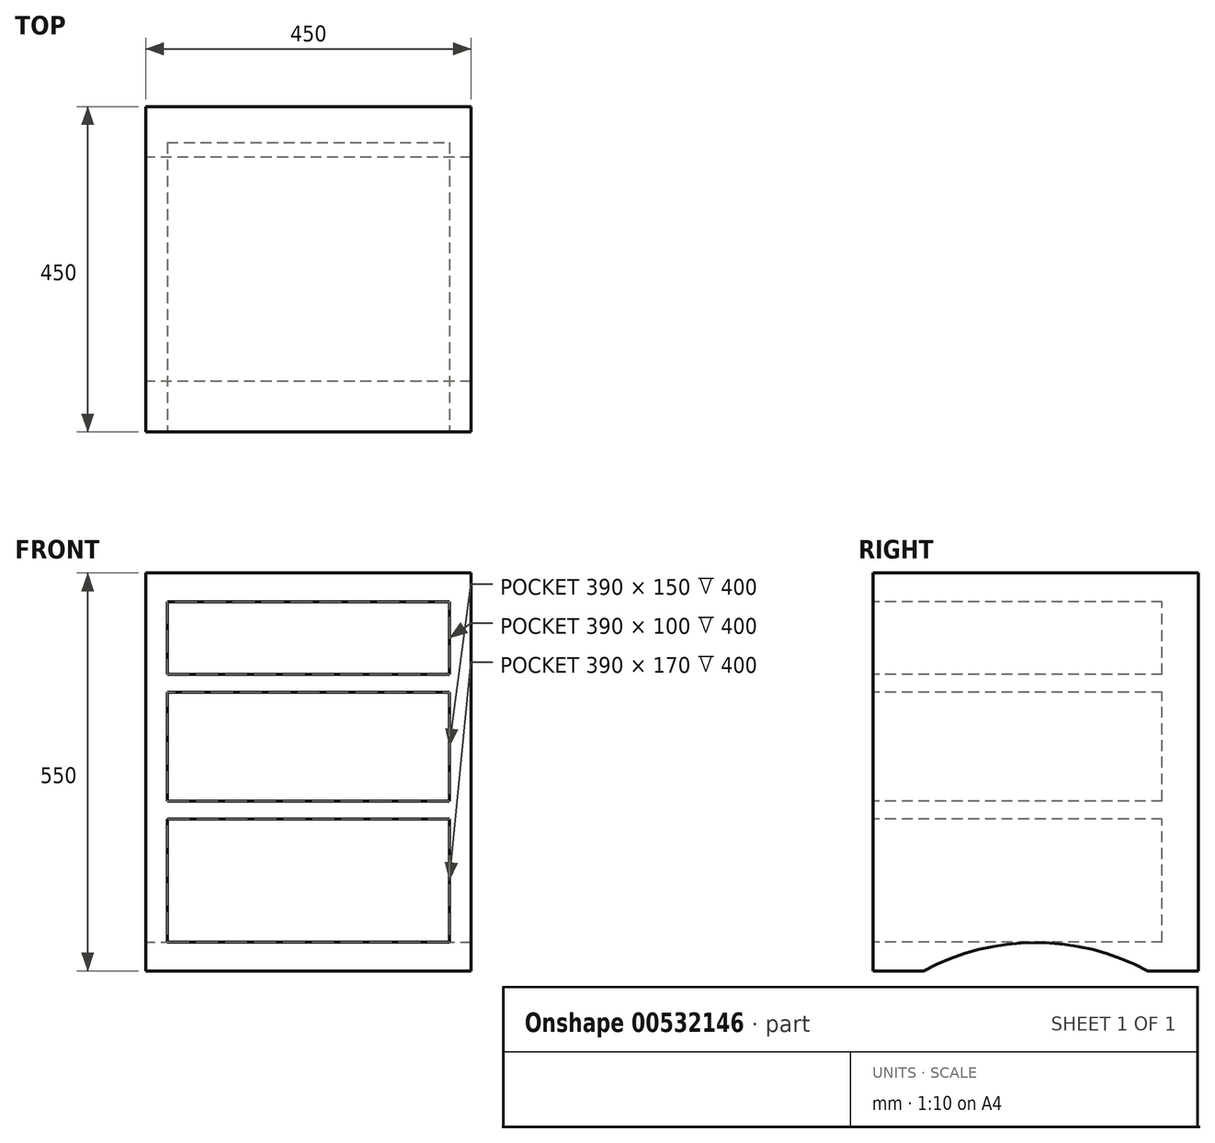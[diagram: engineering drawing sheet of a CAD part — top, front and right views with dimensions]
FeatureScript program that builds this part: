
annotation { "Feature Type Name" : "Feature", "Feature Type Description" : "" }
export const myFeature = defineFeature(function(context is Context, id is Id, definition is map)
    precondition{}
    {
        {
            var Q0;
            Q0=qCreatedBy(makeId("Right.planeOp"),FACE);
            var sketch = newSketch(context, id + "F0", { "sketchPlane" : qUnion([Q0])});
            skLineSegment(sketch, "E0.top", {"start": v(266.1, 549.82) * mm, "end": v(-183.9, 549.82) * mm});
            skLineSegment(sketch, "E0.left", {"start": v(266.1, -0.18) * mm, "end": v(266.1, 549.82) * mm});
            skLineSegment(sketch, "E0.right", {"start": v(-183.9, -0.18) * mm, "end": v(-183.9, 549.82) * mm});
            skArc(sketch, "E1", {"start": v(196.1, -0.18) * mm, "mid": v(41.1, 39.03) * mm, "end": v(-113.9, -0.18) * mm});
            skLineSegment(sketch, "E2", {"start": v(-183.9, -0.18) * mm, "end": v(-113.9, -0.18) * mm});
            skLineSegment(sketch, "E3", {"start": v(196.1, -0.18) * mm, "end": v(266.1, -0.18) * mm});
            skSolve(sketch);
        }
        {
            var Q0;
            Q0=makeQuery(id+"F0.imprint","IMPRINT",FACE,{"disambiguationData":[TD([[makeQuery(id+"F0.imprint","IMPRINT",EDGE,{"derivedFrom":sQuery(id+"F0.wireOp",EDGE,"E0.top")}),1.0]])]});
            extrude(context, id + "F1", {"entities" : qUnion([Q0]), "depth" : 450 * mm, "offsetDistance" : 25 * mm});
        }
        {
            var Q0;
            Q0=makeQuery(id+"F1.opExtrude","SWEPT_FACE",FACE,{"disambiguationData":[OSD([sQuery(id+"F0.wireOp",EDGE,"E0.right")])]});
            var sketch = newSketch(context, id + "F2", { "sketchPlane" : qUnion([Q0])});
            skLineSegment(sketch, "E4.bottom", {"start": v(420, 39.82) * mm, "end": v(30, 39.82) * mm});
            skLineSegment(sketch, "E4.top", {"start": v(420, 509.82) * mm, "end": v(30, 509.82) * mm});
            skLineSegment(sketch, "E4.left", {"start": v(420, 39.82) * mm, "end": v(420, 509.82) * mm});
            skLineSegment(sketch, "E4.right", {"start": v(30, 39.82) * mm, "end": v(30, 509.82) * mm});
            skPoint(sketch, "E4.middle", {"position": v(225, 274.82) * mm});
            skPoint(sketch, "E4.middle.positionSnap0", {"position": v(0, 274.82) * mm});
            skPoint(sketch, "E4.middle.positionSnap1", {"position": v(225, 549.82) * mm});
            skPoint(sketch, "E4.centerSnap0", {"position": v(0, 274.82) * mm});
            skPoint(sketch, "E4.centerSnap1", {"position": v(225, 549.82) * mm});
            skSolve(sketch);
        }
        {
            var Q0;
            Q0=makeQuery(id+"F2.imprint","IMPRINT",FACE,{"disambiguationData":[TD([[makeQuery(id+"F2.imprint","IMPRINT",EDGE,{"derivedFrom":sQuery(id+"F2.wireOp",EDGE,"E4.bottom")}),-1.0]])]});
            extrude(context, id + "F3", {"entities" : qUnion([Q0]), "operationType" : NewBodyOperationType.REMOVE, "oppositeDirection" : true, "depth" : 400 * mm, "offsetDistance" : 25 * mm});
        }
        {
            var Q0;
            Q0=makeQuery(id+"F3.boolean.opBoolean","COPY",FACE,{"derivedFrom":makeQuery(id+"F3.opExtrude","SWEPT_FACE",FACE,{"disambiguationData":[OSD([sQuery(id+"F2.wireOp",EDGE,"E4.left")])]})});
            var sketch = newSketch(context, id + "F4", { "sketchPlane" : qUnion([Q0])});
            skLineSegment(sketch, "E5.bottom", {"start": v(-216.1, 409.82) * mm, "end": v(183.9, 409.82) * mm});
            skLineSegment(sketch, "E5.top", {"start": v(-216.1, 384.82) * mm, "end": v(183.9, 384.82) * mm});
            skLineSegment(sketch, "E5.left", {"start": v(-216.1, 409.82) * mm, "end": v(-216.1, 384.82) * mm});
            skLineSegment(sketch, "E5.right", {"start": v(183.9, 409.82) * mm, "end": v(183.9, 384.82) * mm});
            skLineSegment(sketch, "E6.bottom", {"start": v(-216.1, 234.82) * mm, "end": v(183.9, 234.82) * mm});
            skLineSegment(sketch, "E6.top", {"start": v(-216.1, 209.82) * mm, "end": v(183.9, 209.82) * mm});
            skLineSegment(sketch, "E6.left", {"start": v(-216.1, 234.82) * mm, "end": v(-216.1, 209.82) * mm});
            skLineSegment(sketch, "E6.right", {"start": v(183.9, 234.82) * mm, "end": v(183.9, 209.82) * mm});
            skSolve(sketch);
        }
        {
            var Q0;
            Q0=makeQuery(id+"F4.imprint","IMPRINT",FACE,{"disambiguationData":[TD([[makeQuery(id+"F4.imprint","IMPRINT",EDGE,{"derivedFrom":sQuery(id+"F4.wireOp",EDGE,"E5.bottom")}),-1.0]])]});
            extrude(context, id + "F5", {"entities" : qUnion([Q0]), "operationType" : NewBodyOperationType.ADD, "depth" : 390 * mm, "offsetDistance" : 25 * mm});
        }
        {
            var Q0;
            {var subQ0=sQuery(id+"F2.wireOp",EDGE,"E4.left");var subQ1=sQuery(id+"F2.wireOp",EDGE,"E4.bottom");Q0=makeQuery(id+"F5.boolean.opBoolean","SPLIT",FACE,{"disambiguationData":[TD([makeQuery(id+"F3.boolean.opBoolean","COPY",FACE,{"derivedFrom":makeQuery(id+"F3.opExtrude","SWEPT_FACE",FACE,{"disambiguationData":[OSD([subQ1])]})})])],"derivedFrom":makeQuery(id+"F3.boolean.opBoolean","COPY",FACE,{"derivedFrom":makeQuery(id+"F3.opExtrude","SWEPT_FACE",FACE,{"disambiguationData":[OSD([subQ0])]})})});}
            var sketch = newSketch(context, id + "F6", { "sketchPlane" : qUnion([Q0])});
            skLineSegment(sketch, "E7.bottom", {"start": v(-216.1, 234.82) * mm, "end": v(183.9, 234.82) * mm});
            skLineSegment(sketch, "E7.top", {"start": v(-216.1, 209.82) * mm, "end": v(183.9, 209.82) * mm});
            skLineSegment(sketch, "E7.left", {"start": v(-216.1, 234.82) * mm, "end": v(-216.1, 209.82) * mm});
            skLineSegment(sketch, "E7.right", {"start": v(183.9, 234.82) * mm, "end": v(183.9, 209.82) * mm});
            skSolve(sketch);
        }
        {
            var Q0;
            Q0=makeQuery(id+"F6.imprint","IMPRINT",FACE,{"disambiguationData":[TD([[makeQuery(id+"F6.imprint","IMPRINT",EDGE,{"derivedFrom":sQuery(id+"F6.wireOp",EDGE,"E7.bottom")}),-1.0]])]});
            extrude(context, id + "F7", {"entities" : qUnion([Q0]), "operationType" : NewBodyOperationType.ADD, "depth" : 390 * mm, "offsetDistance" : 25 * mm});
        }
    });
